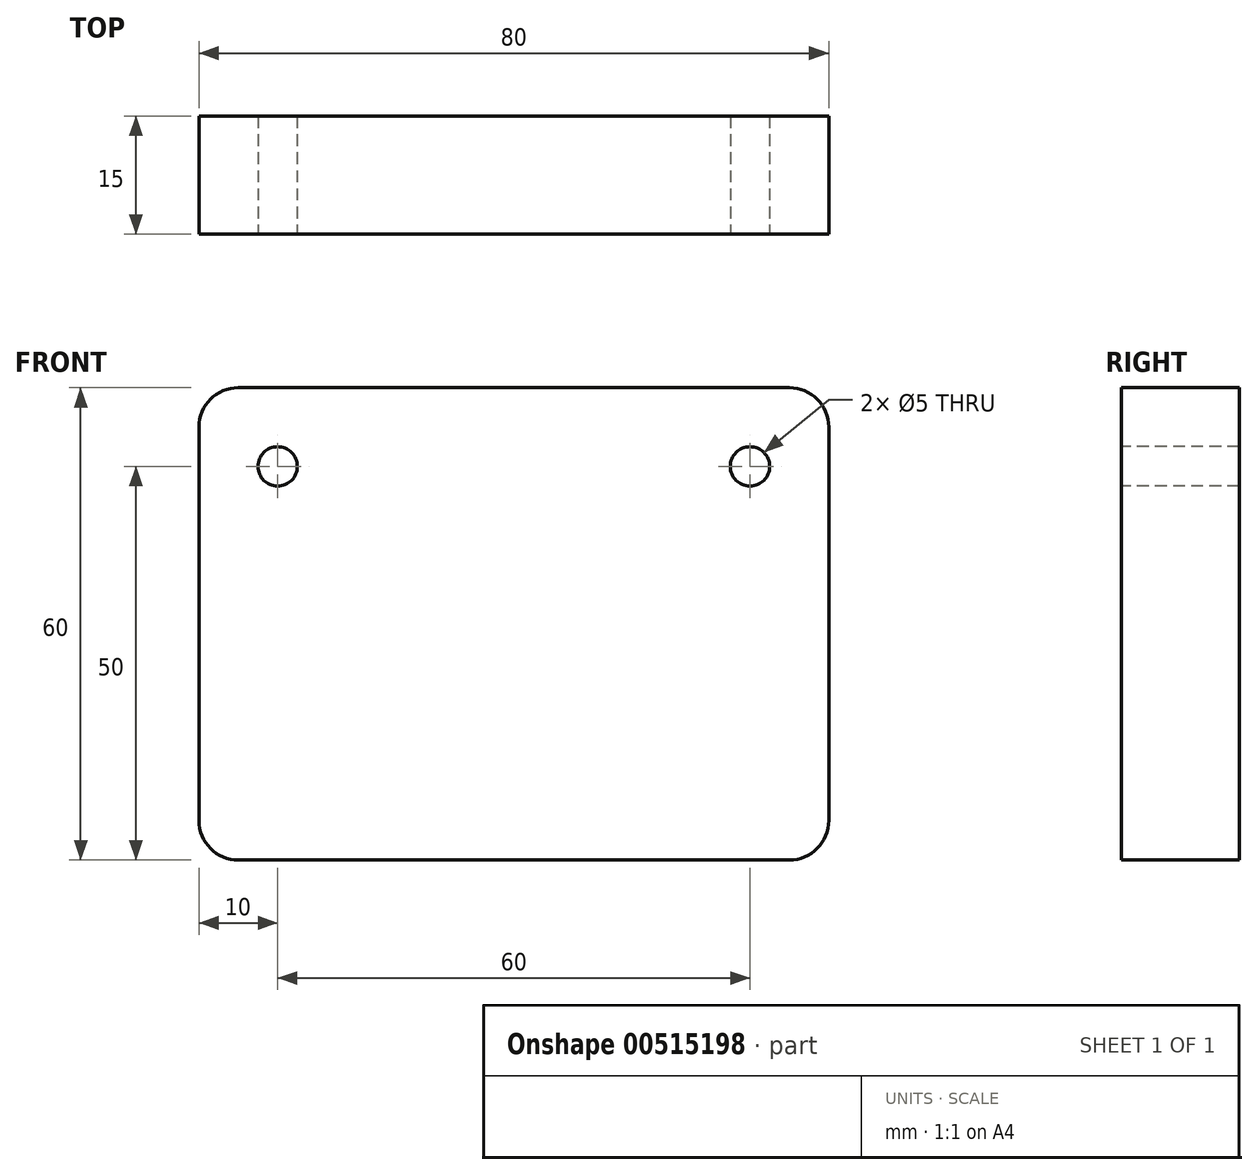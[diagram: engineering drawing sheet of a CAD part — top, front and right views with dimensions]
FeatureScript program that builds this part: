
annotation { "Feature Type Name" : "Feature", "Feature Type Description" : "" }
export const myFeature = defineFeature(function(context is Context, id is Id, definition is map)
    precondition{}
    {
        {
            var Q0;
            Q0=qCreatedBy(makeId("Front.planeOp"),FACE);
            var sketch = newSketch(context, id + "F0", { "sketchPlane" : qUnion([Q0])});
            skLineSegment(sketch, "E0.bottom", {"start": v(40, 30) * mm, "end": v(-40, 30) * mm});
            skLineSegment(sketch, "E0.top", {"start": v(40, -30) * mm, "end": v(-40, -30) * mm});
            skLineSegment(sketch, "E0.left", {"start": v(40, 30) * mm, "end": v(40, -30) * mm});
            skLineSegment(sketch, "E0.right", {"start": v(-40, 30) * mm, "end": v(-40, -30) * mm});
            skPoint(sketch, "E0.middle", {"position": v(0, 0) * mm});
            skSolve(sketch);
        }
        {
            var Q0;
            Q0 = qSketchRegion(id + "F0", true);
            extrude(context, id + "F1", {"entities" : qUnion([Q0]), "depth" : 15 * mm, "offsetDistance" : 25 * mm});
        }
        {
            var Q0;
            Q0=makeQuery(id+"F1.opExtrude","CAP_FACE",FACE,{"disambiguationData":[OSD([sQuery(id+"F0.wireOp",EDGE,"E0.bottom"),sQuery(id+"F0.wireOp",EDGE,"E0.top"),sQuery(id+"F0.wireOp",EDGE,"E0.left"),sQuery(id+"F0.wireOp",EDGE,"E0.right")])],"isStart":false});
            var sketch = newSketch(context, id + "F2", { "sketchPlane" : qUnion([Q0])});
            skLineSegment(sketch, "E1", {"start": v(0, 36.43) * mm, "end": v(0, -39) * mm, "construction": true});
            skPoint(sketch, "E2", {"position": v(-30, 20) * mm});
            skLineSegment(sketch, "E3.0", {"start": v(40, 30) * mm, "end": v(-40, 30) * mm});
            skPoint(sketch, "E4.MirrorP", {"position": v(30, 20) * mm});
            skSolve(sketch);
        }
        {
            var Q0;
            Q0=sQuery(id+"F2.wireOp",VERTEX,"E2");
            var Q1;
            Q1=sQuery(id+"F2.wireOp",VERTEX,"E4.MirrorP");
            var Q2;
            Q2=makeQuery(id+"F1.opExtrude","SWEPT_BODY",BODY,{"disambiguationData":[OSD([sQuery(id+"F0.wireOp",EDGE,"E0.bottom"),sQuery(id+"F0.wireOp",EDGE,"E0.top"),sQuery(id+"F0.wireOp",EDGE,"E0.left"),sQuery(id+"F0.wireOp",EDGE,"E0.right")])]});
            hole(context, id + "F3", {"style" : HoleStyle.SIMPLE, "endStyle" : HoleEndStyle.THROUGH, "standardTappedOrClearance" : lookupTablePath({ "standard" : "ISO", "engagement" : "75%", "pitch" : "1 mm", "size" : "M6", "type" : "Tapped" }), "standardBlindInLast" : lookupTablePath({ "standard" : "ISO", "engagement" : "75%", "pitch" : "1 mm", "size" : "M6", "type" : "Tapped" }), "holeDiameter" : 5 * mm, "showTappedDepth" : true, "isTappedThrough" : true, "tappedDepth" : 12 * mm, "tapClearance" : 3, "startFromSketch" : true, "locations" : qUnion([Q0, Q1]), "scope" : qUnion([Q2]), "majorDiameter" : 6 * mm});
        }
        {
            var Q0;
            Q0=makeQuery(id+"F1.opExtrude","SWEPT_EDGE",EDGE,{"disambiguationData":[OSD([sQuery(id+"F0.wireOp",EDGE,"E0.bottom"),sQuery(id+"F0.wireOp",EDGE,"E0.left")])]});
            var Q1;
            Q1=makeQuery(id+"F1.opExtrude","SWEPT_EDGE",EDGE,{"disambiguationData":[OSD([sQuery(id+"F0.wireOp",EDGE,"E0.bottom"),sQuery(id+"F0.wireOp",EDGE,"E0.right")])]});
            var Q2;
            Q2=makeQuery(id+"F1.opExtrude","SWEPT_EDGE",EDGE,{"disambiguationData":[OSD([sQuery(id+"F0.wireOp",EDGE,"E0.top"),sQuery(id+"F0.wireOp",EDGE,"E0.right")])]});
            var Q3;
            Q3=makeQuery(id+"F1.opExtrude","SWEPT_EDGE",EDGE,{"disambiguationData":[OSD([sQuery(id+"F0.wireOp",EDGE,"E0.top"),sQuery(id+"F0.wireOp",EDGE,"E0.left")])]});
            fillet(context, id + "F4", {"entities" : qUnion([Q0, Q1, Q2, Q3]), "radius" : 5 * mm, "tangentPropagation" : true, "allowEdgeOverflow" : false});
        }
    });
